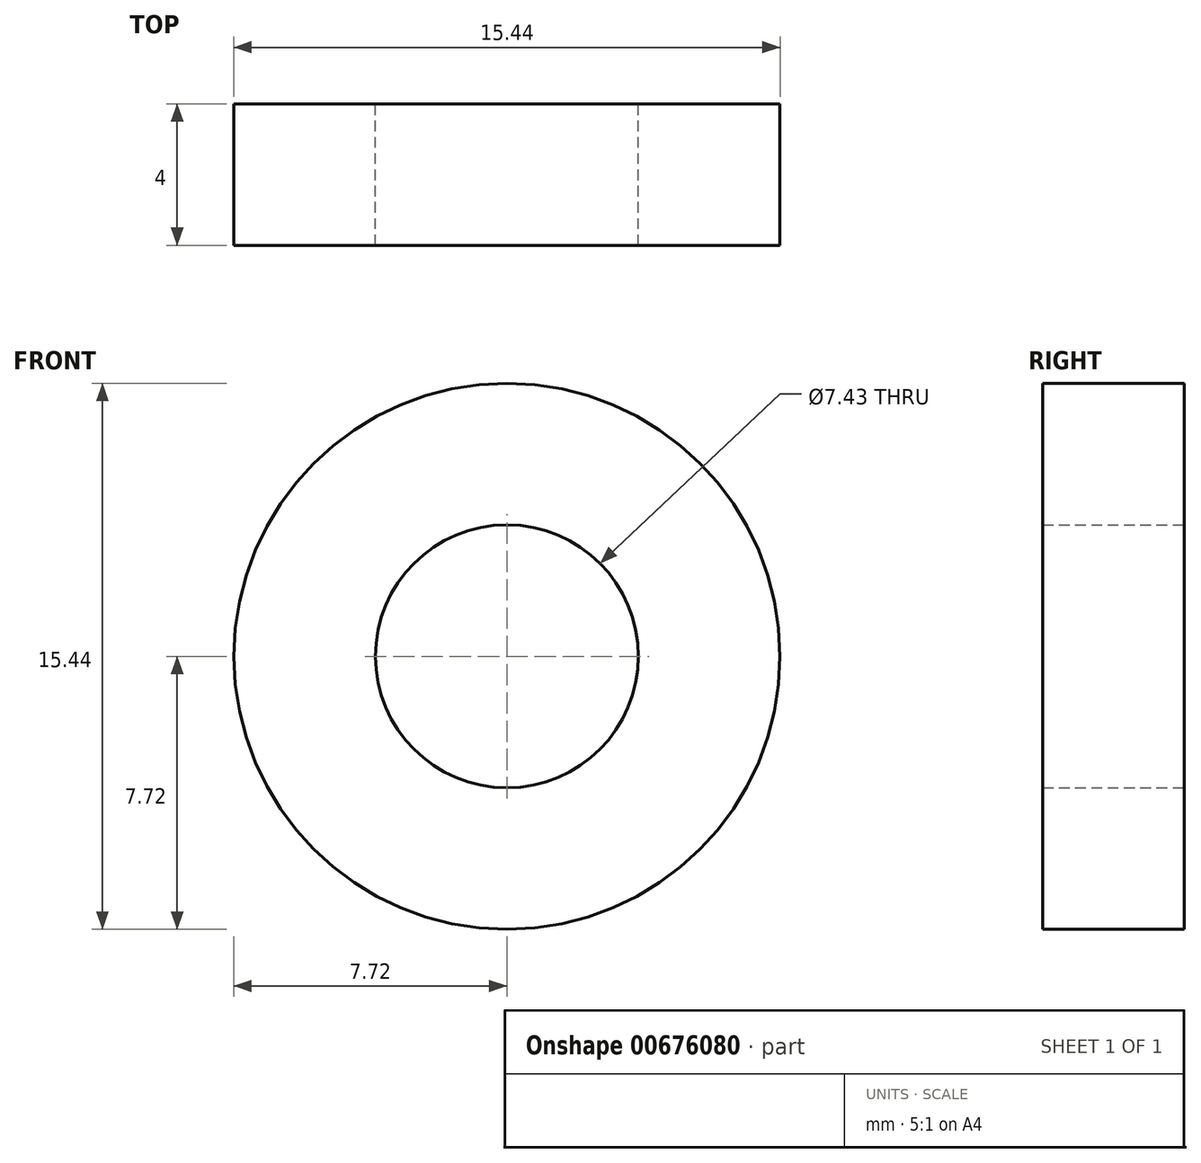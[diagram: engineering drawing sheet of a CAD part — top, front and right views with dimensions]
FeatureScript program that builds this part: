
annotation { "Feature Type Name" : "Feature", "Feature Type Description" : "" }
export const myFeature = defineFeature(function(context is Context, id is Id, definition is map)
    precondition{}
    {
        {
            var Q0;
            Q0=qCreatedBy(makeId("Front.planeOp"),FACE);
            var sketch = newSketch(context, id + "F0", { "sketchPlane" : qUnion([Q0])});
            skCircle(sketch, "E0", {"center": v(0, 0) * mm, "radius": 3.72 * mm});
            skCircle(sketch, "E1.0", {"center": v(0, 0) * mm, "radius": 7.72 * mm});
            skSolve(sketch);
        }
        {
            var Q0;
            Q0=makeQuery(id+"F0.imprint","IMPRINT",FACE,{"disambiguationData":[TD([[makeQuery(id+"F0.imprint","IMPRINT",EDGE,{"derivedFrom":sQuery(id+"F0.wireOp",EDGE,"E0")}),-1.0]])]});
            extrude(context, id + "F1", {"entities" : qUnion([Q0]), "depth" : 4 * mm, "offsetDistance" : 25 * mm});
        }
    });
